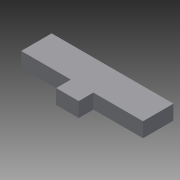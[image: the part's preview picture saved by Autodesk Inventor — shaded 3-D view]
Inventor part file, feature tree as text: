
AUTODESK INVENTOR PART (.ipt)
format: ipt  version: 2013 (Build 170138000, 138)  size: 91,648 bytes
history: native  units: mm
features: other x2, extrude x1, sketch x1
ambient origin geometry x8: Origin, YZ Plane, XZ Plane, XY Plane, X Axis, Y Axis, Z Axis, Center Point
feature tree (4):
  other  "Blocks"
  extrude  "Extrusion6"  Depth=3.0mm
  sketch  "Sketch1"  dims[d0=3.0mm d2=3.0mm d3=0.1mm d7=22.5mm d8=12.4mm d9=4.5mm d10=4.5mm d11=2.0mm d12=2.0mm d59=27.0mm d60=6.75mm d61=5.0mm d62=3.25mm d65=3.25mm d66=0.0mm]
  other  "Block1"
